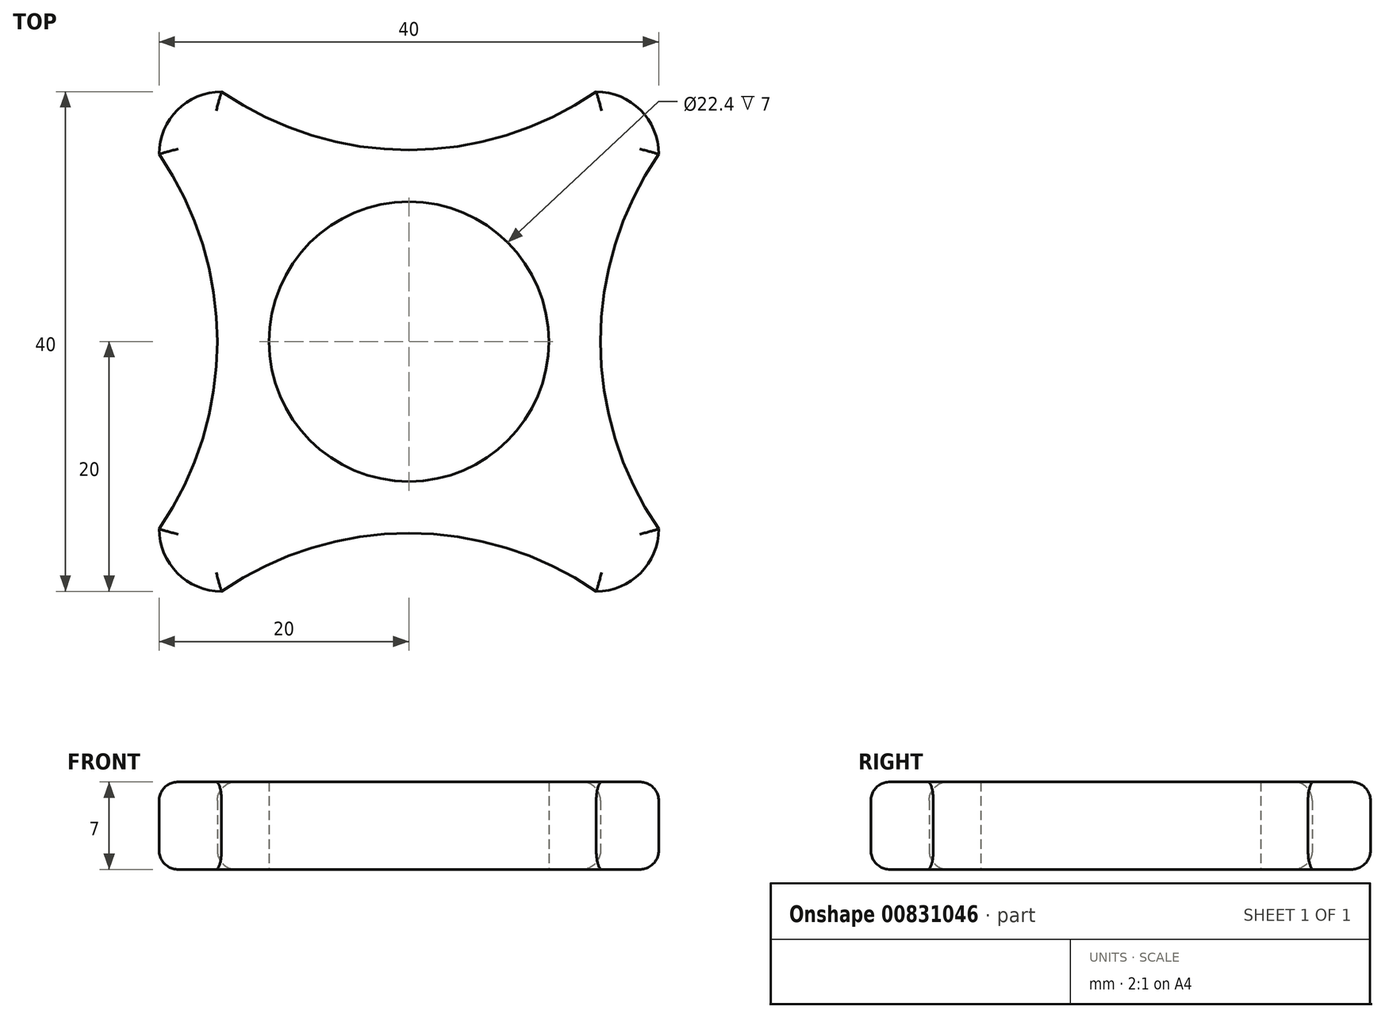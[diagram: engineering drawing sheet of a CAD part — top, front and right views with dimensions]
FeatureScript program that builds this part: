
annotation { "Feature Type Name" : "Feature", "Feature Type Description" : "" }
export const myFeature = defineFeature(function(context is Context, id is Id, definition is map)
    precondition{}
    {
        {
            var Q0;
            Q0=qCreatedBy(makeId("Top.planeOp"),FACE);
            var sketch = newSketch(context, id + "F0", { "sketchPlane" : qUnion([Q0])});
            skCircle(sketch, "E0", {"center": v(0, 0) * mm, "radius": 11.2 * mm});
            skPoint(sketch, "E1.visualSharp", {"position": v(-20, 20) * mm});
            skArc(sketch, "E1.filletArc", {"start": v(-15, 20) * mm, "mid": v(-18.54, 18.54) * mm, "end": v(-20, 15) * mm});
            skPoint(sketch, "E2.visualSharp", {"position": v(20, 20) * mm});
            skArc(sketch, "E2.filletArc", {"start": v(20, 15) * mm, "mid": v(18.54, 18.54) * mm, "end": v(15, 20) * mm});
            skPoint(sketch, "E3.visualSharp", {"position": v(20, -20) * mm});
            skArc(sketch, "E3.filletArc", {"start": v(15, -20) * mm, "mid": v(18.54, -18.54) * mm, "end": v(20, -15) * mm});
            skPoint(sketch, "E4.visualSharp", {"position": v(-20, -20) * mm});
            skArc(sketch, "E4.filletArc", {"start": v(-20, -15) * mm, "mid": v(-18.54, -18.54) * mm, "end": v(-15, -20) * mm});
            skPoint(sketch, "E5.MirrorCS.end.orphan", {"position": v(-20, -15) * mm});
            skPoint(sketch, "E5.MirrorCS.start.orphan", {"position": v(-20, 15) * mm});
            skArc(sketch, "E6", {"start": v(-20, -15) * mm, "mid": v(-15.34, 0) * mm, "end": v(-20, 15) * mm});
            skArc(sketch, "E7.1.0", {"start": v(15, -20) * mm, "mid": v(0, -15.34) * mm, "end": v(-15, -20) * mm});
            skArc(sketch, "E7.2.0", {"start": v(20, 15) * mm, "mid": v(15.34, 0) * mm, "end": v(20, -15) * mm});
            skArc(sketch, "E7.3.0", {"start": v(-15, 20) * mm, "mid": v(0, 15.34) * mm, "end": v(15, 20) * mm});
            skSolve(sketch);
        }
        {
            var Q0;
            Q0=makeQuery(id+"F0.imprint","IMPRINT",FACE,{"disambiguationData":[TD([[makeQuery(id+"F0.imprint","IMPRINT",EDGE,{"derivedFrom":sQuery(id+"F0.wireOp",EDGE,"E0")}),-1.0]])]});
            extrude(context, id + "F1", {"entities" : qUnion([Q0]), "depth" : 7 * mm, "offsetDistance" : 25 * mm});
        }
        {
            var Q0;
            Q0=makeQuery(id+"F1.opExtrude","CAP_EDGE",EDGE,{"disambiguationData":[OSD([sQuery(id+"F0.wireOp",EDGE,"E7.3.0")])],"isStart":false});
            var Q1;
            Q1=makeQuery(id+"F1.opExtrude","CAP_EDGE",EDGE,{"disambiguationData":[OSD([sQuery(id+"F0.wireOp",EDGE,"E2.filletArc")])],"isStart":false});
            var Q2;
            Q2=makeQuery(id+"F1.opExtrude","CAP_EDGE",EDGE,{"disambiguationData":[OSD([sQuery(id+"F0.wireOp",EDGE,"E7.2.0")])],"isStart":false});
            var Q3;
            Q3=makeQuery(id+"F1.opExtrude","CAP_EDGE",EDGE,{"disambiguationData":[OSD([sQuery(id+"F0.wireOp",EDGE,"E3.filletArc")])],"isStart":false});
            var Q4;
            Q4=makeQuery(id+"F1.opExtrude","CAP_EDGE",EDGE,{"disambiguationData":[OSD([sQuery(id+"F0.wireOp",EDGE,"E7.1.0")])],"isStart":false});
            var Q5;
            Q5=makeQuery(id+"F1.opExtrude","CAP_EDGE",EDGE,{"disambiguationData":[OSD([sQuery(id+"F0.wireOp",EDGE,"E4.filletArc")])],"isStart":false});
            var Q6;
            Q6=makeQuery(id+"F1.opExtrude","CAP_EDGE",EDGE,{"disambiguationData":[OSD([sQuery(id+"F0.wireOp",EDGE,"E6")])],"isStart":false});
            var Q7;
            Q7=makeQuery(id+"F1.opExtrude","CAP_EDGE",EDGE,{"disambiguationData":[OSD([sQuery(id+"F0.wireOp",EDGE,"E1.filletArc")])],"isStart":false});
            fillet(context, id + "F2", {"entities" : qUnion([Q0, Q1, Q2, Q3, Q4, Q5, Q6, Q7]), "radius" : 1.5 * mm, "tangentPropagation" : true, "allowEdgeOverflow" : false});
        }
        {
            var Q0;
            Q0=makeQuery(id+"F1.opExtrude","CAP_EDGE",EDGE,{"disambiguationData":[OSD([sQuery(id+"F0.wireOp",EDGE,"E7.1.0")])],"isStart":true});
            var Q1;
            Q1=makeQuery(id+"F1.opExtrude","CAP_EDGE",EDGE,{"disambiguationData":[OSD([sQuery(id+"F0.wireOp",EDGE,"E6")])],"isStart":true});
            var Q2;
            Q2=makeQuery(id+"F1.opExtrude","CAP_EDGE",EDGE,{"disambiguationData":[OSD([sQuery(id+"F0.wireOp",EDGE,"E7.3.0")])],"isStart":true});
            var Q3;
            Q3=makeQuery(id+"F1.opExtrude","CAP_EDGE",EDGE,{"disambiguationData":[OSD([sQuery(id+"F0.wireOp",EDGE,"E7.2.0")])],"isStart":true});
            var Q4;
            Q4=makeQuery(id+"F1.opExtrude","CAP_EDGE",EDGE,{"disambiguationData":[OSD([sQuery(id+"F0.wireOp",EDGE,"E3.filletArc")])],"isStart":true});
            var Q5;
            Q5=makeQuery(id+"F1.opExtrude","CAP_EDGE",EDGE,{"disambiguationData":[OSD([sQuery(id+"F0.wireOp",EDGE,"E4.filletArc")])],"isStart":true});
            var Q6;
            Q6=makeQuery(id+"F1.opExtrude","CAP_EDGE",EDGE,{"disambiguationData":[OSD([sQuery(id+"F0.wireOp",EDGE,"E1.filletArc")])],"isStart":true});
            var Q7;
            Q7=makeQuery(id+"F1.opExtrude","CAP_EDGE",EDGE,{"disambiguationData":[OSD([sQuery(id+"F0.wireOp",EDGE,"E2.filletArc")])],"isStart":true});
            fillet(context, id + "F3", {"entities" : qUnion([Q0, Q1, Q2, Q3, Q4, Q5, Q6, Q7]), "radius" : 1.5 * mm, "tangentPropagation" : true, "allowEdgeOverflow" : false});
        }
    });
